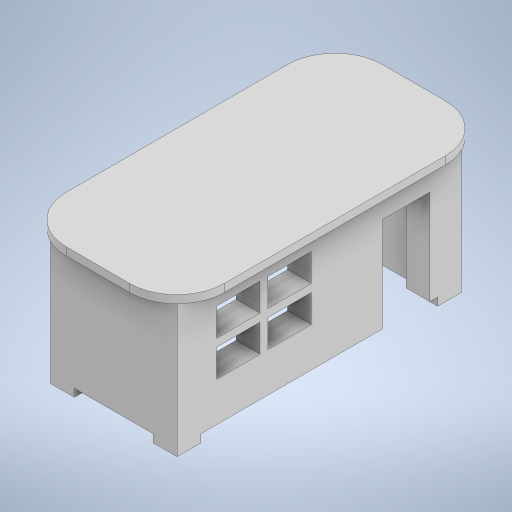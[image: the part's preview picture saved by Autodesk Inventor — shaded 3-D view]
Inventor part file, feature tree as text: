
AUTODESK INVENTOR PART (.ipt)
format: ipt  version: 2023 (Build 270158000, 158)  size: 304,128 bytes
history: native  units: mm
features: extrude x4, sketch x4, fillet x1
ambient origin geometry x8: Origin, YZ Plane, XZ Plane, XY Plane, X Axis, Y Axis, Z Axis, Center Point
bodies: Solid1 (feature_tree)
feature tree (9):
  extrude  "Extrusion1"  Depth=15.0mm
  extrude  "Extrusion2"  Depth=15.0mm
  extrude  "Extrusion3"  Depth=15.0mm
  fillet  "Fillet1"  Radius=150.0mm
  extrude  "Extrusion4"  Depth=5.0mm TaperAngle=0.0deg
  sketch  "Sketch1"  dims[d0=15.0mm d1=15.0mm]
  sketch  "Sketch2"  dims[d2=15.0mm d3=15.0mm]
  sketch  "Sketch3"  dims[d4=15.0mm d5=15.0mm d6=150.0mm]
  sketch  "Sketch4"  dims[d7=50.0mm d8=5.0mm d9=0.0mm d10=80.0mm d11=0.0mm d12=10.0mm d13=10.0mm d14=10.0mm d15=10.0mm d16=5.0mm d17=0.0mm d18=30.0mm d19=60.0mm d20=30.0mm d21=40.0mm d22=60.0mm d23=25.0mm d24=20.0mm d25=0.0mm d26=15.0mm d27=5.0mm d28=5.0mm d29=17.5mm d30=27.5mm d31=15.0mm d32=0.0mm]
